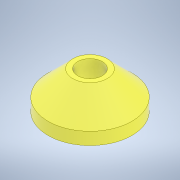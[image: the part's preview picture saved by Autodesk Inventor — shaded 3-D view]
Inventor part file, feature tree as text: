
AUTODESK INVENTOR PART (.ipt)
format: ipt  version: 2021 (Build 250183000, 183)  size: 111,616 bytes
history: native  units: mm
features: other x2, sketch x1
ambient origin geometry x8: Origin, YZ Plane, XZ Plane, XY Plane, X Axis, Y Axis, Z Axis, Center Point
bodies: Body1 (feature_tree)
feature tree (3):
  other  "Sólido1"
  other  "Revolução1"
  sketch  "Esboço1"  dims[d0=34.0mm d1=10.0mm d2=15.0mm d3=10.0mm d4=15.0mm d5=45.0deg d6=90.0deg]
